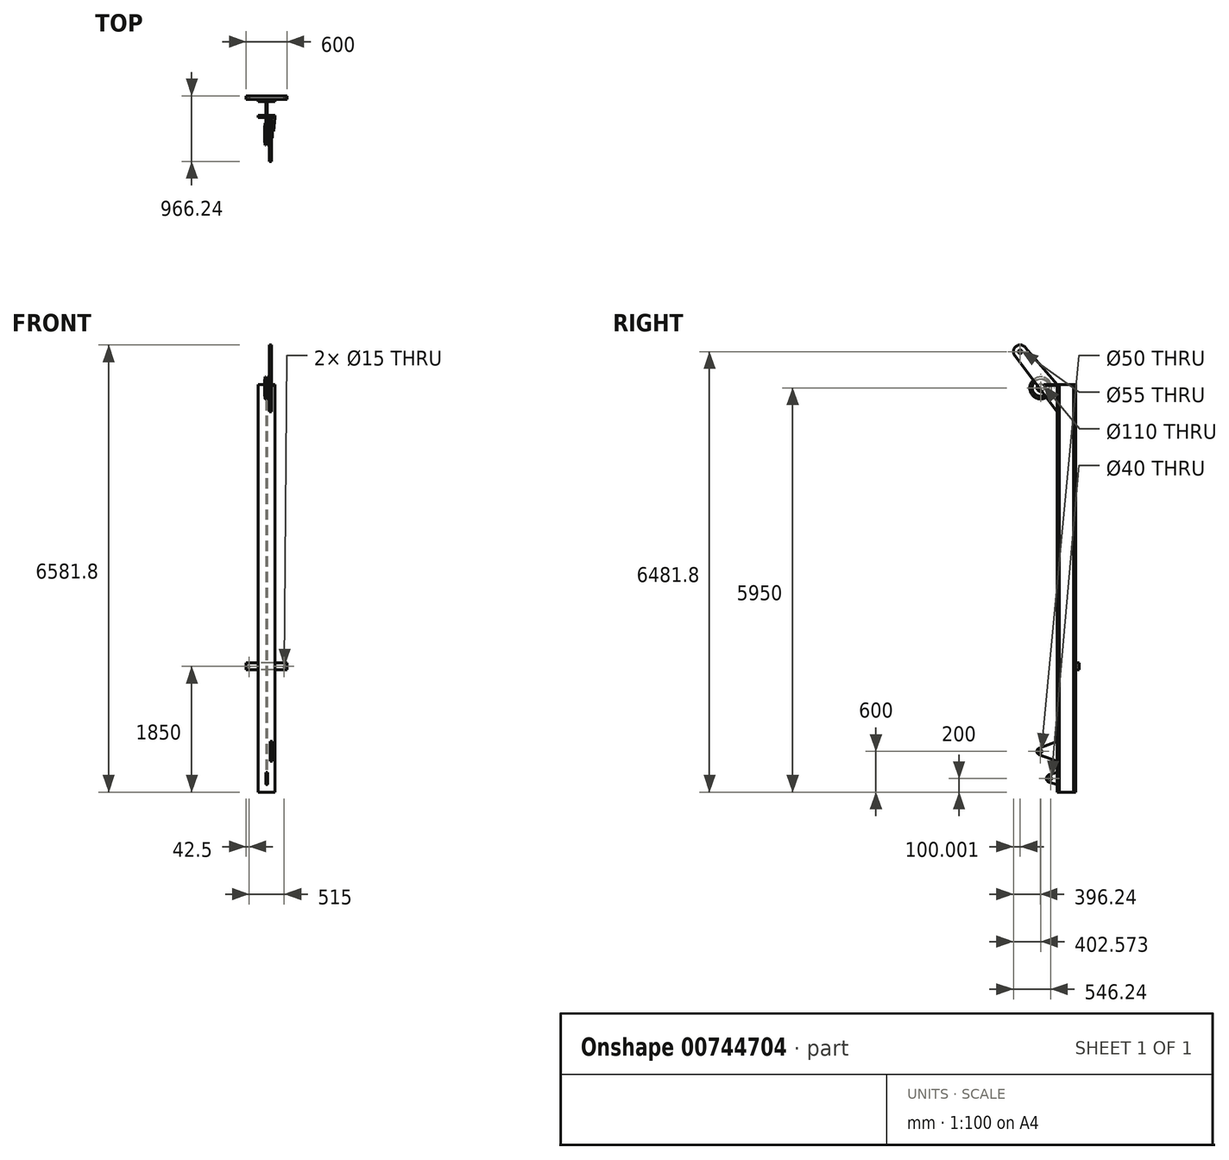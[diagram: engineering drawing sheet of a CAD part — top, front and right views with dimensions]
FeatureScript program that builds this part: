
annotation { "Feature Type Name" : "Feature", "Feature Type Description" : "" }
export const myFeature = defineFeature(function(context is Context, id is Id, definition is map)
    precondition{}
    {
        {
            var Q0;
            Q0=qCreatedBy(makeId("Top.planeOp"),FACE);
            var sketch = newSketch(context, id + "F0", { "sketchPlane" : qUnion([Q0])});
            skLineSegment(sketch, "E0", {"start": v(0, 135) * mm, "end": v(-124, 135) * mm});
            skLineSegment(sketch, "E1", {"start": v(-124, 135) * mm, "end": v(-124, 103) * mm});
            skLineSegment(sketch, "E2", {"start": v(-124, 103) * mm, "end": v(-27, 103) * mm});
            skLineSegment(sketch, "E3", {"start": v(-9, 85) * mm, "end": v(-9, 0) * mm});
            skLineSegment(sketch, "E4.MirrorCS", {"start": v(124, 103) * mm, "end": v(27, 103) * mm});
            skLineSegment(sketch, "E5.MirrorCS", {"start": v(124, 135) * mm, "end": v(124, 103) * mm});
            skLineSegment(sketch, "E6.MirrorCS", {"start": v(9, 85) * mm, "end": v(9, 0) * mm});
            skLineSegment(sketch, "E7.MirrorCS", {"start": v(0, 135) * mm, "end": v(124, 135) * mm});
            skLineSegment(sketch, "E8.MirrorCS", {"start": v(0, -135) * mm, "end": v(124, -135) * mm});
            skLineSegment(sketch, "E9.MirrorCS", {"start": v(9, -85) * mm, "end": v(9, 0) * mm});
            skLineSegment(sketch, "E10.MirrorCS", {"start": v(-124, -135) * mm, "end": v(-124, -103) * mm});
            skLineSegment(sketch, "E11.MirrorCS", {"start": v(124, -103) * mm, "end": v(27, -103) * mm});
            skLineSegment(sketch, "E12.MirrorCS", {"start": v(0, -135) * mm, "end": v(-124, -135) * mm});
            skLineSegment(sketch, "E13.MirrorCS", {"start": v(124, -135) * mm, "end": v(124, -103) * mm});
            skLineSegment(sketch, "E14.MirrorCS", {"start": v(-124, -103) * mm, "end": v(-27, -103) * mm});
            skLineSegment(sketch, "E15.MirrorCS", {"start": v(-9, -85) * mm, "end": v(-9, 0) * mm});
            skLineSegment(sketch, "E16", {"start": v(-9, 103) * mm, "end": v(9, 103) * mm, "construction": true});
            skPoint(sketch, "E17.visualSharp", {"position": v(9, -103) * mm});
            skArc(sketch, "E17.filletArc", {"start": v(9, -85) * mm, "mid": v(14.27, -97.73) * mm, "end": v(27, -103) * mm});
            skPoint(sketch, "E18.visualSharp", {"position": v(-9, -103) * mm});
            skArc(sketch, "E18.filletArc", {"start": v(-27, -103) * mm, "mid": v(-14.27, -97.73) * mm, "end": v(-9, -85) * mm});
            skPoint(sketch, "E19.visualSharp", {"position": v(-9, 103) * mm});
            skArc(sketch, "E19.filletArc", {"start": v(-9, 85) * mm, "mid": v(-14.27, 97.73) * mm, "end": v(-27, 103) * mm});
            skPoint(sketch, "E20.visualSharp", {"position": v(9, 103) * mm});
            skArc(sketch, "E20.filletArc", {"start": v(27, 103) * mm, "mid": v(14.27, 97.73) * mm, "end": v(9, 85) * mm});
            skSolve(sketch);
        }
        {
            var Q0;
            Q0 = qSketchRegion(id + "F0", true);
            extrude(context, id + "F1", {"entities" : qUnion([Q0]), "depth" : 6000 * mm, "offsetDistance" : 25 * mm});
        }
        {
            var Q0;
            Q0=makeQuery(id+"F1.opExtrude","SWEPT_FACE",FACE,{"disambiguationData":[OSD([sQuery(id+"F0.wireOp",EDGE,"E5.MirrorCS")])]});
            var sketch = newSketch(context, id + "F2", { "sketchPlane" : qUnion([Q0])});
            skLineSegment(sketch, "E21", {"start": v(-135, 744.2) * mm, "end": v(-402.1, 646.98) * mm});
            skArc(sketch, "E22", {"start": v(-402.1, 646.98) * mm, "mid": v(-435, 600) * mm, "end": v(-402.1, 553.02) * mm});
            skLineSegment(sketch, "E23", {"start": v(-402.1, 553.02) * mm, "end": v(-135, 455.8) * mm});
            skLineSegment(sketch, "E24", {"start": v(-385, 600) * mm, "end": v(-135, 600) * mm, "construction": true});
            skPoint(sketch, "E25.orphan", {"position": v(135, 6000) * mm});
            skCircle(sketch, "E26", {"center": v(-385, 600) * mm, "radius": 25 * mm});
            skLineSegment(sketch, "E27.0", {"start": v(-135, 6000) * mm, "end": v(-135, 0) * mm});
            skSolve(sketch);
        }
        {
            var Q0;
            Q0 = qSketchRegion(id + "F2", true);
            extrude(context, id + "F3", {"entities" : qUnion([Q0]), "oppositeDirection" : true, "depth" : 70 * mm, "offsetDistance" : 25 * mm, "hasSecondDirection" : true, "secondDirectionOppositeDirection" : true, "secondDirectionDepth" : 40 * mm});
        }
        {
            var Q0;
            Q0=qCreatedBy(makeId("Right.planeOp"),FACE);
            var sketch = newSketch(context, id + "F4", { "sketchPlane" : qUnion([Q0])});
            skCircle(sketch, "E28.0", {"center": v(-378.67, 5950) * mm, "radius": 19.16 * mm});
            skCircle(sketch, "E29", {"center": v(-378.67, 5950) * mm, "radius": 162.5 * mm});
            skSolve(sketch);
        }
        {
            var Q0;
            Q0=makeQuery(id+"F1.opExtrude","SWEPT_FACE",FACE,{"disambiguationData":[OSD([sQuery(id+"F0.wireOp",EDGE,"E0"),sQuery(id+"F0.wireOp",EDGE,"E7.MirrorCS")])]});
            var sketch = newSketch(context, id + "F5", { "sketchPlane" : qUnion([Q0])});
            skLineSegment(sketch, "E30.bottom", {"start": v(-300, 1900) * mm, "end": v(300, 1900) * mm});
            skLineSegment(sketch, "E30.top", {"start": v(-300, 1800) * mm, "end": v(300, 1800) * mm});
            skLineSegment(sketch, "E30.left", {"start": v(-300, 1900) * mm, "end": v(-300, 1800) * mm});
            skLineSegment(sketch, "E30.right", {"start": v(300, 1900) * mm, "end": v(300, 1800) * mm});
            skLineSegment(sketch, "E31.direction1", {"start": v(-300, 1800) * mm, "end": v(-275, 1800) * mm, "construction": true});
            skCircle(sketch, "E32.0", {"center": v(257.5, 1850) * mm, "radius": 7.5 * mm});
            skLineSegment(sketch, "E33", {"start": v(300, 1850) * mm, "end": v(257.5, 1850) * mm, "construction": true});
            skCircle(sketch, "E34.MirrorC", {"center": v(-257.5, 1850) * mm, "radius": 7.5 * mm});
            skSolve(sketch);
        }
        {
            var Q0;
            Q0 = qSketchRegion(id + "F5", true);
            extrude(context, id + "F6", {"entities" : qUnion([Q0]), "depth" : 50 * mm, "offsetDistance" : 25 * mm});
        }
        {
            var Q0;
            Q0=sQuery(id+"F4.wireOp",VERTEX,"E28.0.center");
            var Q1;
            Q1=qCreatedBy(makeId("Top.planeOp"),FACE);
            cPlane(context, id + "F7", {"entities" : qUnion([Q0, Q1]), "cplaneType" : CPlaneType.PLANE_POINT, "offset" : 25 * mm, "width" : 150 * mm, "height" : 150 * mm});
        }
        {
            var Q0;
            Q0=qCreatedBy(makeId("Right.planeOp"),FACE);
            var sketch = newSketch(context, id + "F8", { "sketchPlane" : qUnion([Q0])});
            skLineSegment(sketch, "E35.0", {"start": v(-135, 6000) * mm, "end": v(-135, 0) * mm});
            skLineSegment(sketch, "E36", {"start": v(-135, 288.91) * mm, "end": v(-250.53, 257.96) * mm});
            skArc(sketch, "E37", {"start": v(-250.53, 257.96) * mm, "mid": v(-295, 200) * mm, "end": v(-250.53, 142.04) * mm});
            skLineSegment(sketch, "E38", {"start": v(-250.53, 142.04) * mm, "end": v(-135, 111.09) * mm});
            skLineSegment(sketch, "E39", {"start": v(-235, 200) * mm, "end": v(-135, 200) * mm, "construction": true});
            skCircle(sketch, "E40", {"center": v(-235, 200) * mm, "radius": 20 * mm});
            skSolve(sketch);
        }
        {
            var Q0;
            {var subQ1=sQuery(id+"F8.wireOp",EDGE,"E36");Q0=makeQuery(id+"F8.imprint","IMPRINT",FACE,{"disambiguationData":[TD([[makeQuery(id+"F8.imprint","IMPRINT",EDGE,{"derivedFrom":subQ1}),1.0]])]});}
            extrude(context, id + "F9", {"entities" : qUnion([Q0]), "endBound" : BoundingType.SYMMETRIC, "depth" : 25 * mm, "offsetDistance" : 25 * mm});
        }
        {
            var Q0;
            Q0=qCreatedBy(makeId("Right.planeOp"),FACE);
            var sketch = newSketch(context, id + "F10", { "sketchPlane" : qUnion([Q0])});
            skLineSegment(sketch, "E41.0", {"start": v(-135, 6000) * mm, "end": v(-135, 0) * mm});
            skLineSegment(sketch, "E42", {"start": v(-135, 6000) * mm, "end": v(-605.42, 6547) * mm});
            skArc(sketch, "E43", {"start": v(-605.42, 6547) * mm, "mid": v(-744.17, 6559.5) * mm, "end": v(-760.78, 6421.19) * mm});
            skLineSegment(sketch, "E44", {"start": v(-760.78, 6421.19) * mm, "end": v(-135, 5600) * mm});
            skCircle(sketch, "E45", {"center": v(-681.24, 6481.8) * mm, "radius": 27.5 * mm});
            skSolve(sketch);
        }
        {
            var Q0;
            Q0 = qSketchRegion(id + "F10", true);
            extrude(context, id + "F11", {"entities" : qUnion([Q0]), "depth" : 70 * mm, "offsetDistance" : 25 * mm, "hasSecondDirection" : true, "secondDirectionOppositeDirection" : false, "secondDirectionDepth" : 40 * mm});
        }
        {
            var Q0;
            Q0=makeQuery(id+"F4.imprint","IMPRINT",FACE,{"disambiguationData":[TD([[makeQuery(id+"F4.imprint","IMPRINT",EDGE,{"derivedFrom":sQuery(id+"F4.wireOp",EDGE,"E28.0")}),-1.0]])]});
            extrude(context, id + "F12", {"entities" : qUnion([Q0]), "endBound" : BoundingType.SYMMETRIC, "depth" : 60 * mm, "offsetDistance" : 25 * mm});
        }
        {
            var Q0;
            Q0=qCreatedBy(id+"F7.planeOp",FACE);
            var sketch = newSketch(context, id + "F13", { "sketchPlane" : qUnion([Q0])});
            skLineSegment(sketch, "E46", {"start": v(-30, -378.67) * mm, "end": v(30, -378.67) * mm});
            skLineSegment(sketch, "E47", {"start": v(-39.04, -253.67) * mm, "end": v(-21, -253.67) * mm});
            skLineSegment(sketch, "E48", {"start": v(-21, -253.67) * mm, "end": v(-21, -207.68) * mm});
            skLineSegment(sketch, "E49", {"start": v(-17.43, -207.68) * mm, "end": v(-6.93, -233.04) * mm});
            skArc(sketch, "E50", {"start": v(-6.93, -233.04) * mm, "mid": v(0, -237.67) * mm, "end": v(6.93, -233.04) * mm});
            skLineSegment(sketch, "E51", {"start": v(6.93, -233.04) * mm, "end": v(15.12, -213.27) * mm});
            skLineSegment(sketch, "E52", {"start": v(21, -213.27) * mm, "end": v(21, -253.67) * mm});
            skLineSegment(sketch, "E53", {"start": v(21, -253.67) * mm, "end": v(35.64, -253.67) * mm});
            skLineSegment(sketch, "E54.0", {"start": v(-30, -216.17) * mm, "end": v(-30, -541.17) * mm});
            skLineSegment(sketch, "E55", {"start": v(30, -541.17) * mm, "end": v(-30, -541.17) * mm});
            skLineSegment(sketch, "E56", {"start": v(-30, -216.17) * mm, "end": v(30, -216.17) * mm});
            skLineSegment(sketch, "E57", {"start": v(0, -378.67) * mm, "end": v(0, -216.17) * mm, "construction": true});
            skLineSegment(sketch, "E58.MirrorCS", {"start": v(30, -216.17) * mm, "end": v(30, -541.17) * mm});
            skLineSegment(sketch, "E59", {"start": v(-30, -323.67) * mm, "end": v(30, -323.67) * mm});
            skSolve(sketch);
        }
        {
            var Q0;
            {var subQ0=sQuery(id+"F13.wireOp",EDGE,"E48");var subQ1=sQuery(id+"F13.wireOp",EDGE,"E47");var subQ2=makeQuery(id+"F13.imprint","INTERSECT",VERTEX,{"derivedFrom":[subQ1,subQ0]});Q0=makeQuery(id+"F13.imprint","IMPRINT",FACE,{"disambiguationData":[TD([[makeQuery(id+"F13.imprint","IMPRINT",EDGE,{"disambiguationData":[TD([[subQ2,1.0]])],"derivedFrom":subQ1}),1.0]])]});}
            var Q1;
            {var subQ0=sQuery(id+"F13.wireOp",EDGE,"E50");Q1=makeQuery(id+"F13.imprint","IMPRINT",FACE,{"disambiguationData":[TD([[makeQuery(id+"F13.imprint","IMPRINT",EDGE,{"derivedFrom":subQ0}),1.0]])]});}
            var Q2;
            {var subQ0=sQuery(id+"F13.wireOp",EDGE,"E53");var subQ1=sQuery(id+"F13.wireOp",EDGE,"E52");var subQ2=makeQuery(id+"F13.imprint","INTERSECT",VERTEX,{"derivedFrom":[subQ1,subQ0]});Q2=makeQuery(id+"F13.imprint","IMPRINT",FACE,{"disambiguationData":[TD([[makeQuery(id+"F13.imprint","IMPRINT",EDGE,{"disambiguationData":[TD([[subQ2,1.0]])],"derivedFrom":subQ1}),1.0]])]});}
            var Q3;
            {var subQ0=sQuery(id+"F13.wireOp",EDGE,"E46");Q3=makeQuery(id+"F13.imprint","IMPRINT",FACE,{"disambiguationData":[TD([[makeQuery(id+"F13.imprint","IMPRINT",EDGE,{"derivedFrom":subQ0}),1.0]])]});}
            var Q4;
            Q4=sQuery(id+"F13.wireOp",EDGE,"E46");
            revolve(context, id + "F14", {"operationType" : NewBodyOperationType.REMOVE, "surfaceOperationType" : NewSurfaceOperationType.NEW, "entities" : qUnion([Q0, Q1, Q2, Q3]), "axis" : qUnion([Q4]), "revolveType" : RevolveType.FULL, "oppositeDirection" : true});
        }
        {
            var Q0;
            Q0=makeQuery(id+"F1.opExtrude","CAP_FACE",FACE,{"disambiguationData":[OSD([sQuery(id+"F0.wireOp",EDGE,"E0"),sQuery(id+"F0.wireOp",EDGE,"E1"),sQuery(id+"F0.wireOp",EDGE,"E2"),sQuery(id+"F0.wireOp",EDGE,"E3"),sQuery(id+"F0.wireOp",EDGE,"E4.MirrorCS"),sQuery(id+"F0.wireOp",EDGE,"E5.MirrorCS"),sQuery(id+"F0.wireOp",EDGE,"E6.MirrorCS"),sQuery(id+"F0.wireOp",EDGE,"E7.MirrorCS"),sQuery(id+"F0.wireOp",EDGE,"E8.MirrorCS"),sQuery(id+"F0.wireOp",EDGE,"E9.MirrorCS"),sQuery(id+"F0.wireOp",EDGE,"E10.MirrorCS"),sQuery(id+"F0.wireOp",EDGE,"E11.MirrorCS"),sQuery(id+"F0.wireOp",EDGE,"E12.MirrorCS"),sQuery(id+"F0.wireOp",EDGE,"E13.MirrorCS"),sQuery(id+"F0.wireOp",EDGE,"E14.MirrorCS"),sQuery(id+"F0.wireOp",EDGE,"E15.MirrorCS")])],"isStart":false});
            var sketch = newSketch(context, id + "F15", { "sketchPlane" : qUnion([Q0])});
            skLineSegment(sketch, "E60", {"start": v(70, -335.08) * mm, "end": v(70, -135) * mm});
            skLineSegment(sketch, "E61", {"start": v(70, -135) * mm, "end": v(124, -135) * mm});
            skLineSegment(sketch, "E62", {"start": v(124, -135) * mm, "end": v(104.46, -335.08) * mm});
            skLineSegment(sketch, "E63", {"start": v(104.46, -335.08) * mm, "end": v(70, -335.08) * mm});
            skPoint(sketch, "E64.orphan", {"position": v(70, -417.29) * mm});
            skSolve(sketch);
        }
        {
            var Q0;
            Q0=makeQuery(id+"F15.imprint","IMPRINT",FACE,{"disambiguationData":[TD([[makeQuery(id+"F15.imprint","IMPRINT",EDGE,{"derivedFrom":sQuery(id+"F15.wireOp",EDGE,"E60")}),-1.0]])]});
            extrude(context, id + "F16", {"entities" : qUnion([Q0]), "oppositeDirection" : true, "depth" : 15 * mm, "offsetDistance" : 25 * mm});
        }
    });
